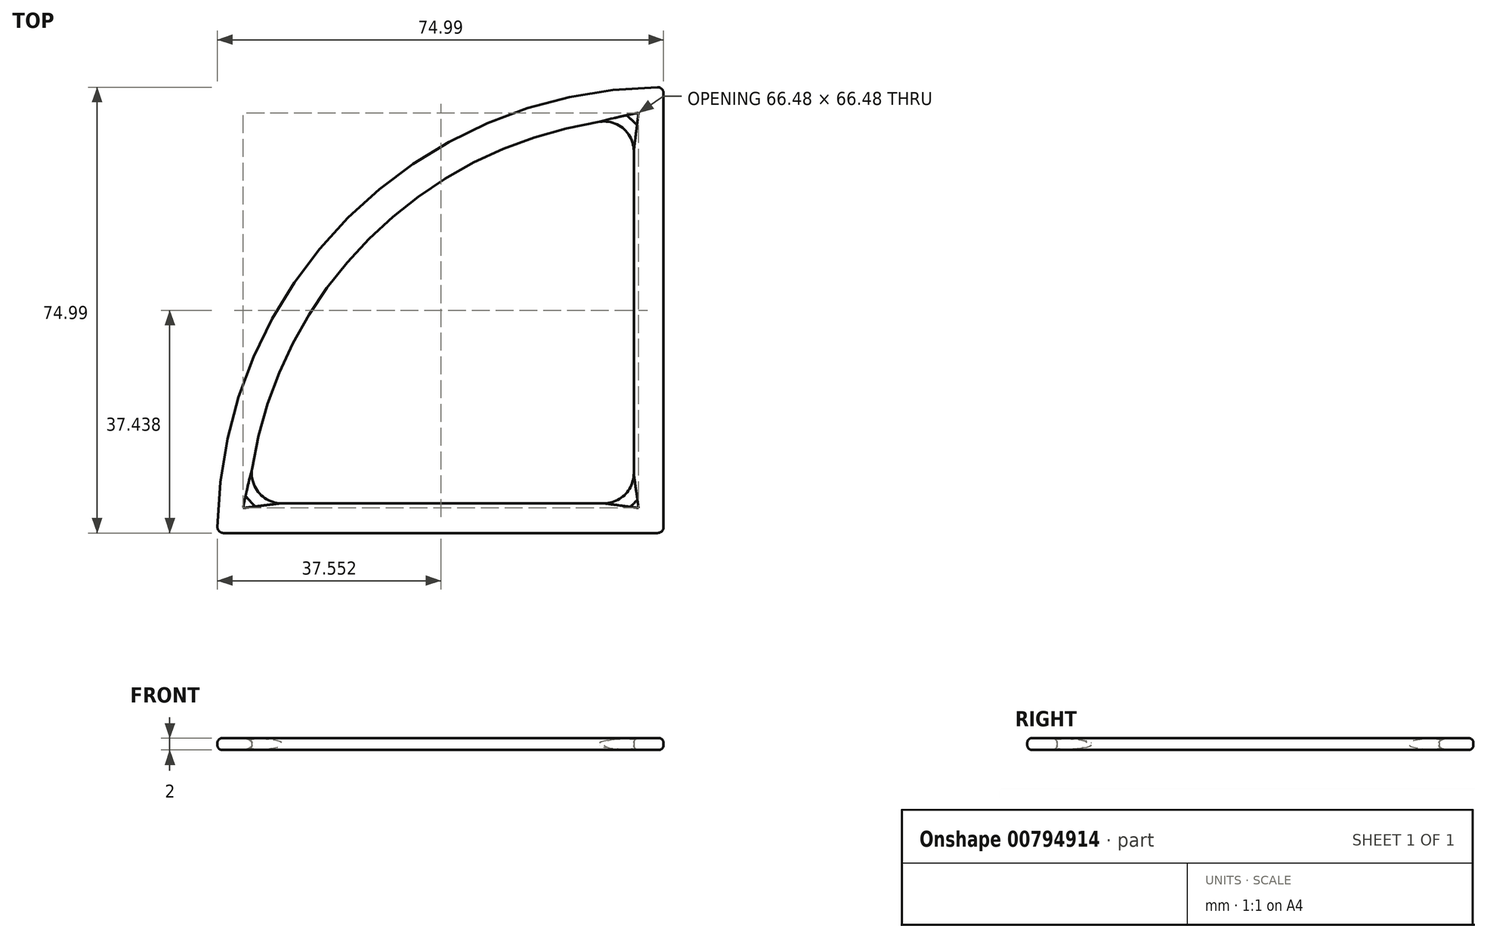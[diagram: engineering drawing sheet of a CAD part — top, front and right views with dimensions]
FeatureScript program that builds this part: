
annotation { "Feature Type Name" : "Feature", "Feature Type Description" : "" }
export const myFeature = defineFeature(function(context is Context, id is Id, definition is map)
    precondition{}
    {
        {
            var Q0;
            Q0=qCreatedBy(makeId("Top.planeOp"),FACE);
            var sketch = newSketch(context, id + "F0", { "sketchPlane" : qUnion([Q0])});
            skLineSegment(sketch, "E0", {"start": v(0, 0) * mm, "end": v(-75, 0) * mm});
            skLineSegment(sketch, "E1", {"start": v(0, 0) * mm, "end": v(0, 75) * mm});
            skArc(sketch, "E2", {"start": v(0, 75) * mm, "mid": v(-53.03, 53.03) * mm, "end": v(-75, 0) * mm});
            skLineSegment(sketch, "E3.0", {"start": v(-5, 5) * mm, "end": v(-69.82, 5) * mm});
            skLineSegment(sketch, "E3.1", {"start": v(-5, 5) * mm, "end": v(-5, 69.82) * mm});
            skArc(sketch, "E3.2", {"start": v(-5, 69.82) * mm, "mid": v(-49.5, 49.5) * mm, "end": v(-69.82, 5) * mm});
            skSolve(sketch);
        }
        {
            var Q0;
            Q0=makeQuery(id+"F0.imprint","IMPRINT",FACE,{"disambiguationData":[TD([[makeQuery(id+"F0.imprint","IMPRINT",EDGE,{"derivedFrom":sQuery(id+"F0.wireOp",EDGE,"E0")}),-1.0]])]});
            extrude(context, id + "F1", {"entities" : qUnion([Q0]), "depth" : 2 * mm, "offsetDistance" : 25 * mm});
        }
        {
            var Q0;
            Q0=makeQuery(id+"F1.opExtrude","CAP_FACE",FACE,{"disambiguationData":[OSD([sQuery(id+"F0.wireOp",EDGE,"E0"),sQuery(id+"F0.wireOp",EDGE,"E1"),sQuery(id+"F0.wireOp",EDGE,"E2"),sQuery(id+"F0.wireOp",EDGE,"E3.0"),sQuery(id+"F0.wireOp",EDGE,"E3.1"),sQuery(id+"F0.wireOp",EDGE,"E3.2")])],"isStart":false});
            var Q1;
            Q1=makeQuery(id+"F1.opExtrude","CAP_FACE",FACE,{"disambiguationData":[OSD([sQuery(id+"F0.wireOp",EDGE,"E0"),sQuery(id+"F0.wireOp",EDGE,"E1"),sQuery(id+"F0.wireOp",EDGE,"E2"),sQuery(id+"F0.wireOp",EDGE,"E3.0"),sQuery(id+"F0.wireOp",EDGE,"E3.1"),sQuery(id+"F0.wireOp",EDGE,"E3.2")])],"isStart":true});
            fillet(context, id + "F2", {"entities" : qUnion([Q0, Q1]), "radius" : 0.8 * mm, "tangentPropagation" : true, "allowEdgeOverflow" : false});
        }
        {
            var Q0;
            Q0=makeQuery(id+"F1.opExtrude","SWEPT_EDGE",EDGE,{"disambiguationData":[OSD([sQuery(id+"F0.wireOp",EDGE,"E0"),sQuery(id+"F0.wireOp",EDGE,"E2")])]});
            var Q1;
            Q1=makeQuery(id+"F1.opExtrude","SWEPT_EDGE",EDGE,{"disambiguationData":[OSD([sQuery(id+"F0.wireOp",EDGE,"E0"),sQuery(id+"F0.wireOp",EDGE,"E1")])]});
            var Q2;
            Q2=makeQuery(id+"F1.opExtrude","SWEPT_EDGE",EDGE,{"disambiguationData":[OSD([sQuery(id+"F0.wireOp",EDGE,"E1"),sQuery(id+"F0.wireOp",EDGE,"E2")])]});
            fillet(context, id + "F3", {"entities" : qUnion([Q0, Q1, Q2]), "radius" : 1 * mm, "tangentPropagation" : true, "allowEdgeOverflow" : false});
        }
        {
            var Q0;
            Q0=makeQuery(id+"F1.opExtrude","SWEPT_EDGE",EDGE,{"disambiguationData":[OSD([sQuery(id+"F0.wireOp",EDGE,"E3.0"),sQuery(id+"F0.wireOp",EDGE,"E3.2")])]});
            var Q1;
            Q1=makeQuery(id+"F1.opExtrude","SWEPT_EDGE",EDGE,{"disambiguationData":[OSD([sQuery(id+"F0.wireOp",EDGE,"E3.1"),sQuery(id+"F0.wireOp",EDGE,"E3.2")])]});
            var Q2;
            Q2=makeQuery(id+"F1.opExtrude","SWEPT_EDGE",EDGE,{"disambiguationData":[OSD([sQuery(id+"F0.wireOp",EDGE,"E3.0"),sQuery(id+"F0.wireOp",EDGE,"E3.1")])]});
            fillet(context, id + "F4", {"entities" : qUnion([Q0, Q1, Q2]), "radius" : 5 * mm, "tangentPropagation" : true, "allowEdgeOverflow" : false});
        }
    });
